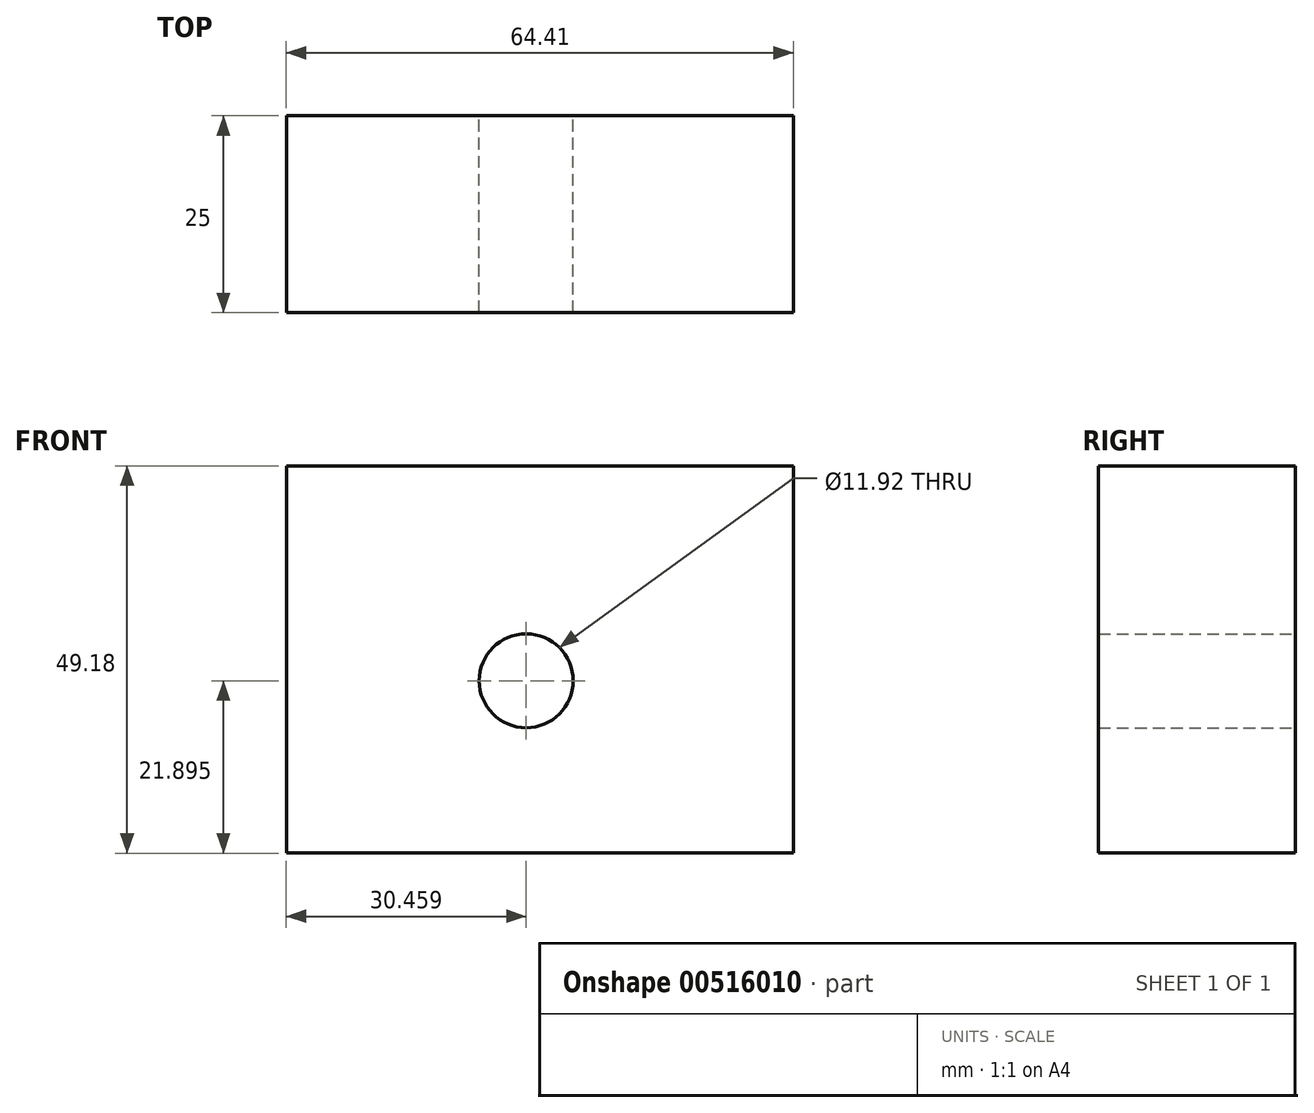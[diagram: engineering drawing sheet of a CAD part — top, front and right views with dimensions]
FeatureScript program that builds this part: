
annotation { "Feature Type Name" : "Feature", "Feature Type Description" : "" }
export const myFeature = defineFeature(function(context is Context, id is Id, definition is map)
    precondition{}
    {
        {
            var Q0;
            Q0=qCreatedBy(makeId("Front.planeOp"),FACE);
            var sketch = newSketch(context, id + "F0", { "sketchPlane" : qUnion([Q0])});
            skLineSegment(sketch, "E0.bottom", {"start": v(-112.63, 38.23) * mm, "end": v(-48.22, 38.23) * mm});
            skLineSegment(sketch, "E0.top", {"start": v(-112.63, -10.95) * mm, "end": v(-48.22, -10.95) * mm});
            skLineSegment(sketch, "E0.left", {"start": v(-112.63, 38.23) * mm, "end": v(-112.63, -10.95) * mm});
            skLineSegment(sketch, "E0.right", {"start": v(-48.22, 38.23) * mm, "end": v(-48.22, -10.95) * mm});
            skCircle(sketch, "E1", {"center": v(-82.17, 10.95) * mm, "radius": 5.96 * mm});
            skSolve(sketch);
        }
        {
            var Q0;
            Q0 = qSketchRegion(id + "F0", true);
            extrude(context, id + "F1", {"entities" : qUnion([Q0]), "depth" : 25 * mm, "offsetDistance" : 25 * mm});
        }
    });
